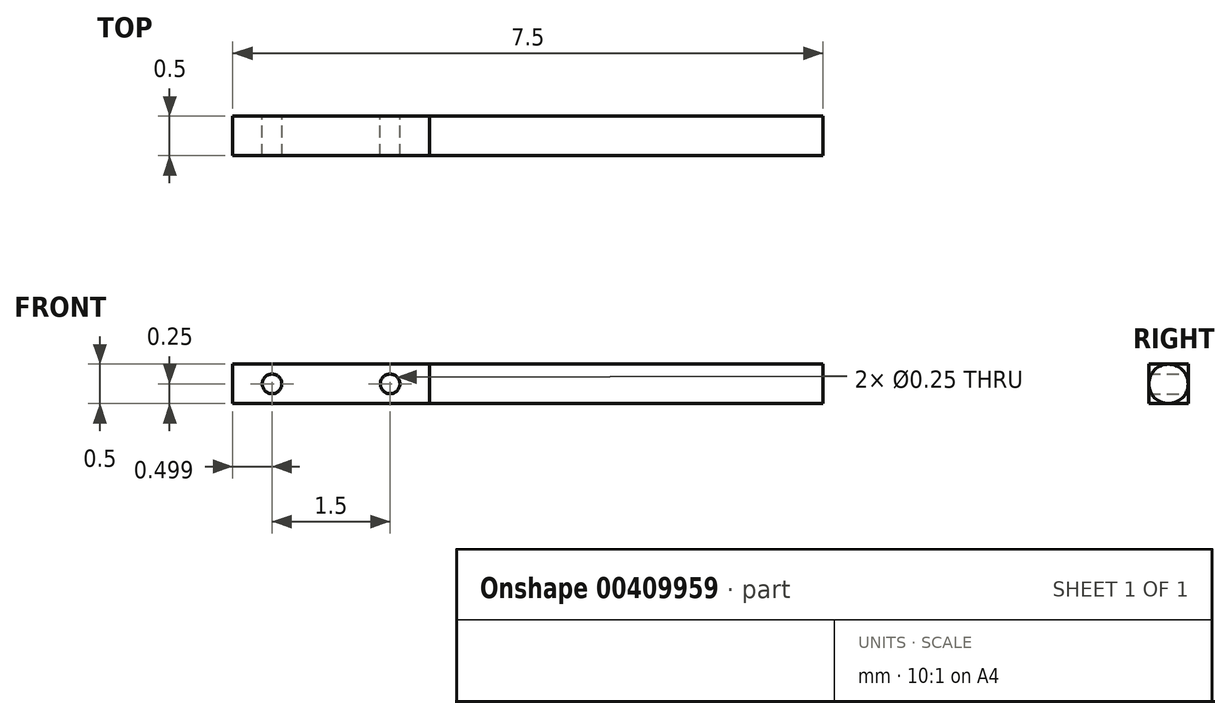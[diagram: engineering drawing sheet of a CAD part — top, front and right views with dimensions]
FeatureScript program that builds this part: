
annotation { "Feature Type Name" : "Feature", "Feature Type Description" : "" }
export const myFeature = defineFeature(function(context is Context, id is Id, definition is map)
    precondition{}
    {
        {
            var Q0;
            Q0=qCreatedBy(makeId("Front.planeOp"),FACE);
            var sketch = newSketch(context, id + "F0", { "sketchPlane" : qUnion([Q0])});
            skLineSegment(sketch, "E0", {"start": v(-26.3, 0.5) * mm, "end": v(-23.8, 0.5) * mm});
            skLineSegment(sketch, "E1", {"start": v(-23.8, 0.5) * mm, "end": v(-23.8, 0) * mm});
            skLineSegment(sketch, "E2", {"start": v(-23.8, 0) * mm, "end": v(-26.3, 0) * mm});
            skLineSegment(sketch, "E3", {"start": v(-26.3, 0) * mm, "end": v(-26.3, 0.5) * mm});
            skCircle(sketch, "E4", {"center": v(-25.8, 0.25) * mm, "radius": 0.12 * mm});
            skCircle(sketch, "E5", {"center": v(-24.3, 0.25) * mm, "radius": 0.13 * mm});
            skSolve(sketch);
        }
        {
            var Q0;
            Q0=makeQuery(id+"F0.imprint","IMPRINT",FACE,{"disambiguationData":[TD([[makeQuery(id+"F0.imprint","IMPRINT",EDGE,{"derivedFrom":sQuery(id+"F0.wireOp",EDGE,"E0")}),-1.0]])]});
            extrude(context, id + "F1", {"entities" : qUnion([Q0]), "endBound" : BoundingType.SYMMETRIC, "depth" : 0.5 * mm});
        }
        {
            var Q0;
            Q0=makeQuery(id+"F1.opExtrude","SWEPT_FACE",FACE,{"disambiguationData":[OSD([sQuery(id+"F0.wireOp",EDGE,"E1")])]});
            var sketch = newSketch(context, id + "F2", { "sketchPlane" : qUnion([Q0])});
            skCircle(sketch, "E6", {"center": v(0, 0.25) * mm, "radius": 0.25 * mm});
            skSolve(sketch);
        }
        {
            var Q0;
            {var subQ0=sQuery(id+"F2.wireOp",EDGE,"E6");var subQ1=sQuery(id+"F0.wireOp",EDGE,"E1");var subQ3=makeQuery(id+"F2.imprint","INTERSECT",VERTEX,{"derivedFrom":[makeQuery(id+"F1.opExtrude","CAP_EDGE",EDGE,{"disambiguationData":[OSD([subQ1])],"isStart":true}),subQ0]});Q0=makeQuery(id+"F2.imprint","IMPRINT",FACE,{"disambiguationData":[TD([[makeQuery(id+"F2.imprint","IMPRINT",EDGE,{"disambiguationData":[TD([[subQ3,-1.0]])],"derivedFrom":subQ0}),1.0]])]});}
            extrude(context, id + "F3", {"entities" : qUnion([Q0]), "operationType" : NewBodyOperationType.ADD, "depth" : 5 * mm});
        }
    });
